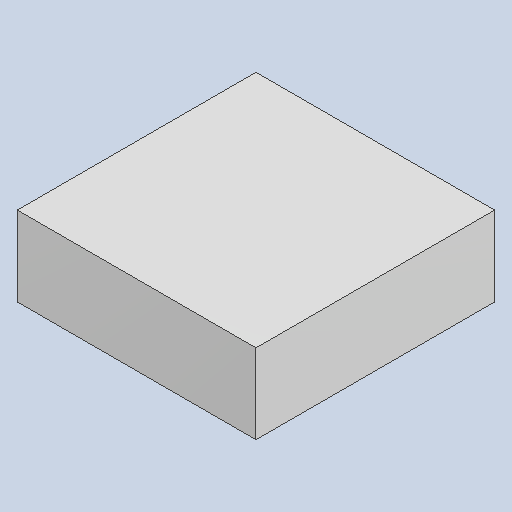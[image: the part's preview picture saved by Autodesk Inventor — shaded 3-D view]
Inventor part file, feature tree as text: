
AUTODESK INVENTOR PART (.ipt)
format: ipt  version: 2023.4 (Build 274418000, 418)  size: 79,872 bytes
history: native  units: mm
features: extrude x1
ambient origin geometry x8: Origin, YZ Plane, XZ Plane, XY Plane, X Axis, Y Axis, Z Axis, Center Point
bodies: Solid1 (feature_tree)
feature tree (1):
  extrude  "Extruded_50"  [1 undecoded]
note: 1 required parameter value undecoded (feature->parameter linkage not recoverable at this tier; creation-order binding heuristic only, values carry confidence <= 0.55)
